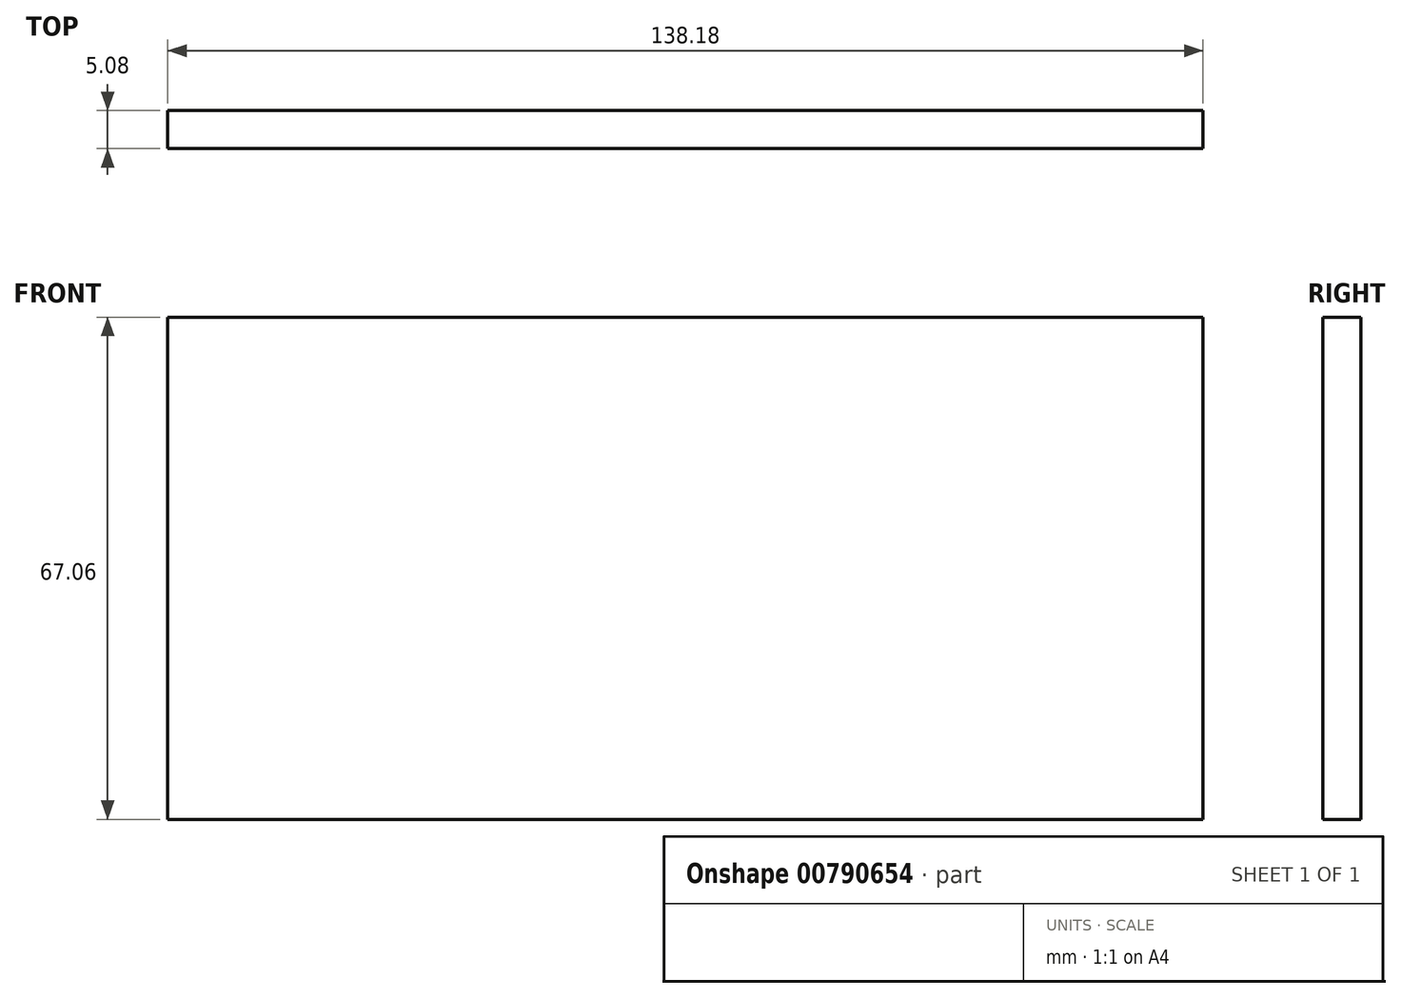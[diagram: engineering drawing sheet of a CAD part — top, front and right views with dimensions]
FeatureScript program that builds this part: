
annotation { "Feature Type Name" : "Feature", "Feature Type Description" : "" }
export const myFeature = defineFeature(function(context is Context, id is Id, definition is map)
    precondition{}
    {
        {
            var Q0;
            Q0=qCreatedBy(makeId("Front.planeOp"),FACE);
            var sketch = newSketch(context, id + "F0", { "sketchPlane" : qUnion([Q0])});
            skLineSegment(sketch, "E0.bottom", {"start": v(1.62, 0) * mm, "end": v(139.8, 0) * mm});
            skLineSegment(sketch, "E0.top", {"start": v(1.62, 67.06) * mm, "end": v(139.8, 67.06) * mm});
            skLineSegment(sketch, "E0.left", {"start": v(1.62, 0) * mm, "end": v(1.62, 67.06) * mm});
            skLineSegment(sketch, "E0.right", {"start": v(139.8, 0) * mm, "end": v(139.8, 67.06) * mm});
            skSolve(sketch);
        }
        {
            var Q0;
            Q0 = qSketchRegion(id + "F0", true);
            extrude(context, id + "F1", {"entities" : qUnion([Q0]), "depth" : 5.08 * mm, "offsetDistance" : 25.4 * mm});
        }
    });
